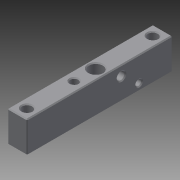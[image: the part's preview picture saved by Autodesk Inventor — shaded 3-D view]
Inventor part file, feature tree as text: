
AUTODESK INVENTOR PART (.ipt)
format: ipt  version: 2015 (Build 190159000, 159)  size: 151,552 bytes
history: native  units: in
note: dims shown in document units (in); Inventor stores cm internally (conversion verified against a paired STEP export)
features: extrude x3, sketch x3, chamfer x2
ambient origin geometry x8: Origin, YZ Plane, XZ Plane, XY Plane, X Axis, Y Axis, Z Axis, Center Point
bodies: Solid1 (feature_tree)
feature tree (8):
  extrude  "Extrusion1"  Depth=1.0in
  chamfer  "Chamfer1"  Distance=4.625in
  extrude  "Extrusion2"  Depth=0.125in
  extrude  "Extrusion3"  Depth=0.125in
  chamfer  "Chamfer2"  Distance=2.125in
  sketch  "Sketch1"  dims[d0=0.625in d1=1.0in d2=4.625in d3=0.0in]
  sketch  "Sketch2"  dims[d4=0.03in d5=0.125in d6=45.0deg d7=0.3125in]
  sketch  "Sketch3"  dims[d8=0.3125in d9=2.8125in d10=2.125in d11=0.3125in d12=0.3125in d13=0.25in d14=0.4375in d15=0.3125in d16=4.625in d17=0.0in d18=1.0625in d19=0.219in d20=0.6875in d21=1.625in d22=0.25in d23=0.1875in d24=4.625in d25=0.0in d26=0.03in d27=0.125in d28=45.0deg]
